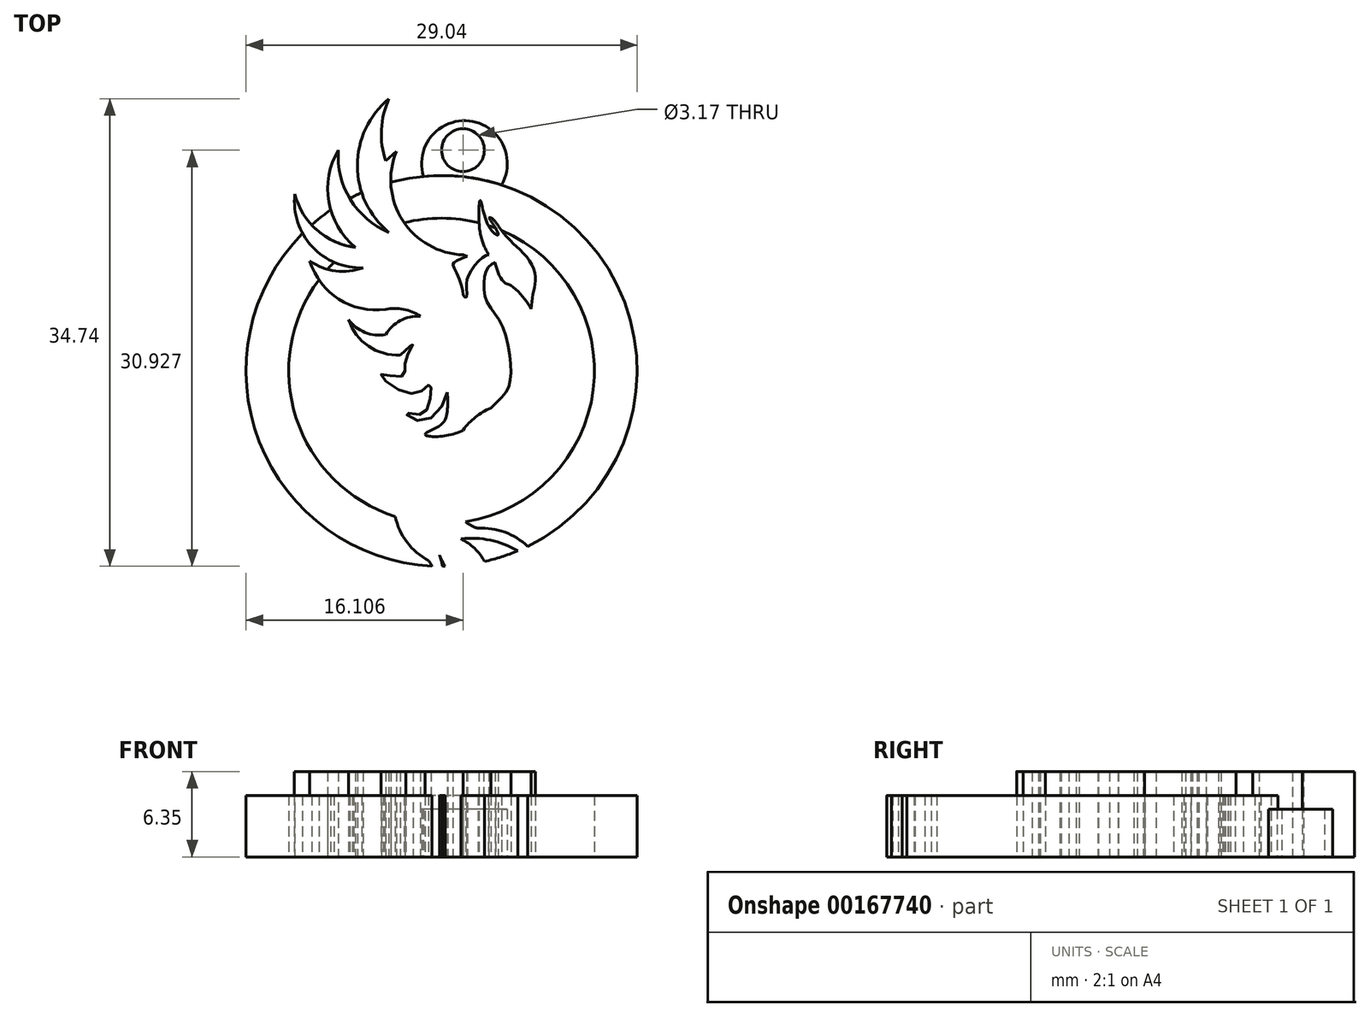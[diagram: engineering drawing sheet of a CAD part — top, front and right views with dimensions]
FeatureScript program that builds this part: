
annotation { "Feature Type Name" : "Feature", "Feature Type Description" : "" }
export const myFeature = defineFeature(function(context is Context, id is Id, definition is map)
    precondition{}
    {
        {
            var Q0;
            Q0=qCreatedBy(makeId("Top.planeOp"),FACE);
            var sketch = newSketch(context, id + "F0", { "sketchPlane" : qUnion([Q0])});
            skArc(sketch, "E0", {"start": v(-8.61, 61.48) * mm, "mid": v(-8.14, 56.34) * mm, "end": v(-3.65, 53.79) * mm});
            skLineSegment(sketch, "E1", {"start": v(-8.61, 61.48) * mm, "end": v(-9.42, 60.77) * mm});
            skArc(sketch, "E2", {"start": v(-9.17, 65.38) * mm, "mid": v(-9.73, 63.1) * mm, "end": v(-9.42, 60.77) * mm});
            skArc(sketch, "E3", {"start": v(-9.17, 65.38) * mm, "mid": v(-11.52, 60.42) * mm, "end": v(-9.17, 55.46) * mm});
            skArc(sketch, "E4", {"start": v(-12.92, 61.58) * mm, "mid": v(-12.04, 57.91) * mm, "end": v(-9.17, 55.46) * mm});
            skArc(sketch, "E5", {"start": v(-12.92, 61.58) * mm, "mid": v(-13.64, 57.73) * mm, "end": v(-11.65, 54.34) * mm});
            skArc(sketch, "E6", {"start": v(-16.16, 58.3) * mm, "mid": v(-14.51, 55.62) * mm, "end": v(-11.65, 54.34) * mm});
            skArc(sketch, "E7", {"start": v(-16.16, 58.3) * mm, "mid": v(-14.88, 54.4) * mm, "end": v(-11.1, 52.83) * mm});
            skArc(sketch, "E8", {"start": v(-15.04, 53.33) * mm, "mid": v(-13.13, 52.59) * mm, "end": v(-11.1, 52.83) * mm});
            skArc(sketch, "E9", {"start": v(-15.04, 53.33) * mm, "mid": v(-12.9, 50.5) * mm, "end": v(-9.42, 49.74) * mm});
            skArc(sketch, "E10", {"start": v(-6.84, 49.23) * mm, "mid": v(-8.08, 49.74) * mm, "end": v(-9.42, 49.74) * mm});
            skArc(sketch, "E11", {"start": v(-6.84, 49.23) * mm, "mid": v(-8.32, 48.9) * mm, "end": v(-9.42, 47.85) * mm});
            skArc(sketch, "E12", {"start": v(-12.17, 48.97) * mm, "mid": v(-10.95, 48.03) * mm, "end": v(-9.42, 47.85) * mm});
            skArc(sketch, "E13", {"start": v(-12.17, 48.97) * mm, "mid": v(-10.7, 47) * mm, "end": v(-8.31, 46.34) * mm});
            skFitSpline(sketch, "E14", {"points": [v(-8.31, 46.34) * mm, v(-7.37, 47.16) * mm, v(-7.94, 46) * mm, v(-7.96, 45.2) * mm, v(-8.31, 44.72) * mm, v(-9.75, 44.89) * mm, v(-8.31, 43.68) * mm, v(-6.63, 43.75) * mm, v(-6.11, 44.15) * mm, v(-6.14, 42.96) * mm, v(-6.8, 41.92) * mm, v(-7.92, 42.02) * mm, v(-6.65, 41.44) * mm, v(-4.84, 43.58) * mm, v(-5.26, 45.16) * mm], "startDerivative": vector(19.86, 19.37) * mm, "endDerivative": vector(-9.99, 17.2) * mm});
            skFitSpline(sketch, "E15", {"points": [v(-4.84, 43.58) * mm, v(-4.84, 42.15) * mm, v(-5.35, 41.13) * mm, v(-6.5, 40.44) * mm, v(-4.37, 40.47) * mm, v(-1.61, 42.4) * mm, v(-0.37, 43.75) * mm, v(-0.15, 45.73) * mm, v(-0.87, 48.75) * mm, v(-1.9, 50.32) * mm, v(-2.1, 51.85) * mm, v(-1.78, 52.89) * mm, v(-1.27, 53.21) * mm], "startDerivative": vector(0.88, -19.52) * mm, "endDerivative": vector(11.24, 4.77) * mm});
            skFitSpline(sketch, "E16", {"points": [v(-1.27, 53.21) * mm, v(-0.99, 52.28) * mm, v(-0.47, 51.65) * mm, v(-0.25, 51.58) * mm, v(0.66, 50.81) * mm, v(1.39, 49.76) * mm], "startDerivative": vector(0.87, -4.4) * mm, "endDerivative": vector(2.52, -4.27) * mm});
            skFitSpline(sketch, "E17", {"points": [v(1.39, 49.76) * mm, v(1.53, 50.91) * mm, v(1.71, 52) * mm, v(1.19, 53.47) * mm, v(-0.13, 54.82) * mm, v(-0.8, 55.59) * mm, v(-1.55, 56.53) * mm, v(-1.77, 56.54) * mm], "startDerivative": vector(0.67, 7.98) * mm, "endDerivative": vector(-3.06, -0.8) * mm});
            skFitSpline(sketch, "E18", {"points": [v(-1.77, 56.54) * mm, v(-1.35, 55.94) * mm, v(-1.07, 55.27) * mm, v(-1.77, 55.93) * mm, v(-2.4, 57.82) * mm, v(-2.43, 55.65) * mm, v(-1.77, 53.8) * mm], "startDerivative": vector(3.16, -4.2) * mm, "endDerivative": vector(4.07, -7.46) * mm});
            skFitSpline(sketch, "E19", {"points": [v(-1.77, 53.8) * mm, v(-2.3, 53.53) * mm, v(-3.21, 52.33) * mm, v(-3.41, 51.45) * mm, v(-3.41, 50.65) * mm, v(-3.59, 50.68) * mm, v(-3.8, 51.57) * mm, v(-4.4, 53.02) * mm, v(-4.34, 53.21) * mm, v(-3.41, 53.68) * mm], "startDerivative": vector(-5.14, -1.6) * mm, "endDerivative": vector(9.08, 3.98) * mm});
            skLineSegment(sketch, "E20", {"start": v(-3.65, 53.79) * mm, "end": v(-3.35, 53.68) * mm});
            skArc(sketch, "E21", {"start": v(-6.89, 39.78) * mm, "mid": v(-8.33, 38.55) * mm, "end": v(-8.97, 36.76) * mm});
            skArc(sketch, "E22", {"start": v(-10.13, 35.15) * mm, "mid": v(-9.37, 35.82) * mm, "end": v(-8.97, 36.76) * mm});
            skArc(sketch, "E23", {"start": v(-10.13, 35.15) * mm, "mid": v(-9.28, 35.35) * mm, "end": v(-8.74, 36.03) * mm});
            skArc(sketch, "E24", {"start": v(-8.74, 36.03) * mm, "mid": v(-8.28, 33.15) * mm, "end": v(-6.23, 31.07) * mm});
            skArc(sketch, "E25", {"start": v(-5.92, 27.33) * mm, "mid": v(-5.55, 29.24) * mm, "end": v(-6.23, 31.07) * mm});
            skArc(sketch, "E26", {"start": v(-5.92, 27.33) * mm, "mid": v(-5.17, 29.34) * mm, "end": v(-5.42, 31.48) * mm});
            skArc(sketch, "E27", {"start": v(-5.42, 31.48) * mm, "mid": v(-4.3, 29.83) * mm, "end": v(-2.56, 28.86) * mm});
            skArc(sketch, "E28", {"start": v(-2.56, 28.86) * mm, "mid": v(-2.81, 26) * mm, "end": v(-1.52, 23.43) * mm});
            skArc(sketch, "E29", {"start": v(-1.52, 28.86) * mm, "mid": v(-1.97, 26.14) * mm, "end": v(-1.52, 23.43) * mm});
            skArc(sketch, "E30", {"start": v(-1.52, 28.86) * mm, "mid": v(-2.12, 31.1) * mm, "end": v(-3.82, 32.67) * mm});
            skArc(sketch, "E31", {"start": v(2.54, 29.7) * mm, "mid": v(-0.21, 32.1) * mm, "end": v(-3.82, 32.67) * mm});
            skArc(sketch, "E32", {"start": v(2.54, 29.7) * mm, "mid": v(0.68, 32.5) * mm, "end": v(-2.56, 33.46) * mm});
            skArc(sketch, "E33", {"start": v(-4.3, 35.51) * mm, "mid": v(-3.74, 34.22) * mm, "end": v(-2.56, 33.46) * mm});
            skArc(sketch, "E34", {"start": v(-1.52, 34.45) * mm, "mid": v(-2.75, 35.38) * mm, "end": v(-4.3, 35.51) * mm});
            skArc(sketch, "E35", {"start": v(-1.52, 34.45) * mm, "mid": v(-2.66, 36.04) * mm, "end": v(-4.52, 36.64) * mm});
            skArc(sketch, "E36", {"start": v(-6.5, 40.44) * mm, "mid": v(-6.73, 40.13) * mm, "end": v(-6.89, 39.78) * mm});
            skArc(sketch, "E37", {"start": v(-5.2, 30.64) * mm, "mid": v(-5.1, 30.64) * mm, "end": v(-4.99, 30.64) * mm});
            skArc(sketch, "E38", {"start": v(-14.37, 51.93) * mm, "mid": v(-16.07, 41.68) * mm, "end": v(-8.7, 34.34) * mm});
            skArc(sketch, "E39.trimOffspring", {"start": v(-13.24, 53.23) * mm, "mid": v(-13.5, 52.98) * mm, "end": v(-13.74, 52.71) * mm});
            skArc(sketch, "E40.trimOffspring", {"start": v(-11.78, 54.45) * mm, "mid": v(-11.83, 54.42) * mm, "end": v(-11.89, 54.38) * mm});
            skArc(sketch, "E41.trimOffspring", {"start": v(-9.46, 55.7) * mm, "mid": v(-9.53, 55.68) * mm, "end": v(-9.6, 55.65) * mm});
            skArc(sketch, "E42.trimOffspring", {"start": v(-2.48, 56.17) * mm, "mid": v(-5.25, 56.51) * mm, "end": v(-8.03, 56.17) * mm});
            skArc(sketch, "E43.trimOffspring", {"start": v(-1.26, 55.78) * mm, "mid": v(-1.52, 55.88) * mm, "end": v(-1.79, 55.97) * mm});
            skArc(sketch, "E44.trimOffspring", {"start": v(-3.48, 33.95) * mm, "mid": v(6, 43.77) * mm, "end": v(-0.81, 55.6) * mm});
            skArc(sketch, "E45.trimOffspring", {"start": v(-2.06, 31) * mm, "mid": v(-0.82, 31.34) * mm, "end": v(0.39, 31.78) * mm});
            skArc(sketch, "E46.trimOffspring", {"start": v(1.13, 32.12) * mm, "mid": v(8.33, 50.26) * mm, "end": v(-9.03, 59.18) * mm});
            skCircle(sketch, "E47", {"center": v(-3.67, 61.57) * mm, "radius": 1.59 * mm});
            skArc(sketch, "E48.trimOffspring", {"start": v(-15.58, 55.37) * mm, "mid": v(-18.8, 39.9) * mm, "end": v(-5.97, 30.66) * mm});
            skArc(sketch, "E49.trimOffspring", {"start": v(-13.5, 57.12) * mm, "mid": v(-14.22, 56.59) * mm, "end": v(-14.91, 56.01) * mm});
            skArc(sketch, "E50.trimOffspring", {"start": v(-11.2, 58.41) * mm, "mid": v(-11.64, 58.2) * mm, "end": v(-12.08, 57.98) * mm});
            skArc(sketch, "E51", {"start": v(-0.8, 58.98) * mm, "mid": v(-3.21, 63.74) * mm, "end": v(-6.6, 59.62) * mm});
            skLineSegment(sketch, "E52", {"start": v(-3.35, 53.68) * mm, "end": v(-3.41, 53.68) * mm});
            skArc(sketch, "E53", {"start": v(-1.61, 42.4) * mm, "mid": v(-4.1, 40.05) * mm, "end": v(-4.52, 36.64) * mm});
            skSolve(sketch);
        }
        {
            var Q0;
            {var subQ1=sQuery(id+"F0.wireOp",EDGE,"E42.trimOffspring");Q0=makeQuery(id+"F0.imprint","IMPRINT",FACE,{"disambiguationData":[TD([[makeQuery(id+"F0.imprint","IMPRINT",EDGE,{"derivedFrom":subQ1}),-1.0]])]});}
            var Q1;
            {var subQ3=sQuery(id+"F0.wireOp",EDGE,"E38");Q1=makeQuery(id+"F0.imprint","IMPRINT",FACE,{"disambiguationData":[TD([[makeQuery(id+"F0.imprint","IMPRINT",EDGE,{"derivedFrom":subQ3}),-1.0]])]});}
            var Q2;
            {var subQ0=sQuery(id+"F0.wireOp",EDGE,"E40.trimOffspring");Q2=makeQuery(id+"F0.imprint","IMPRINT",FACE,{"disambiguationData":[TD([[makeQuery(id+"F0.imprint","IMPRINT",EDGE,{"derivedFrom":subQ0}),-1.0]])]});}
            var Q3;
            {var subQ0=sQuery(id+"F0.wireOp",EDGE,"E41.trimOffspring");Q3=makeQuery(id+"F0.imprint","IMPRINT",FACE,{"disambiguationData":[TD([[makeQuery(id+"F0.imprint","IMPRINT",EDGE,{"derivedFrom":subQ0}),-1.0]])]});}
            var Q4;
            {var subQ3=sQuery(id+"F0.wireOp",EDGE,"E45.trimOffspring");Q4=makeQuery(id+"F0.imprint","IMPRINT",FACE,{"disambiguationData":[TD([[makeQuery(id+"F0.imprint","IMPRINT",EDGE,{"derivedFrom":subQ3}),1.0]])]});}
            var Q5;
            {var subQ3=sQuery(id+"F0.wireOp",EDGE,"E37");Q5=makeQuery(id+"F0.imprint","IMPRINT",FACE,{"disambiguationData":[TD([[makeQuery(id+"F0.imprint","IMPRINT",EDGE,{"derivedFrom":subQ3}),1.0]])]});}
            extrude(context, id + "F1", {"entities" : qUnion([Q0, Q1, Q2, Q3, Q4, Q5]), "depth" : 4.57 * mm});
        }
        {
            var Q0;
            {var subQ53=sQuery(id+"F0.wireOp",EDGE,"E1");Q0=makeQuery(id+"F0.imprint","IMPRINT",FACE,{"disambiguationData":[TD([[makeQuery(id+"F0.imprint","IMPRINT",EDGE,{"derivedFrom":subQ53}),1.0]])]});}
            extrude(context, id + "F2", {"entities" : qUnion([Q0]), "operationType" : NewBodyOperationType.ADD, "depth" : 6.35 * mm});
        }
        {
            var Q0;
            Q0=makeQuery(id+"F0.imprint","IMPRINT",FACE,{"disambiguationData":[TD([[makeQuery(id+"F0.imprint","IMPRINT",EDGE,{"derivedFrom":sQuery(id+"F0.wireOp",EDGE,"E47")}),-1.0]])]});
            extrude(context, id + "F3", {"entities" : qUnion([Q0]), "operationType" : NewBodyOperationType.ADD, "depth" : 3.56 * mm});
        }
    });
